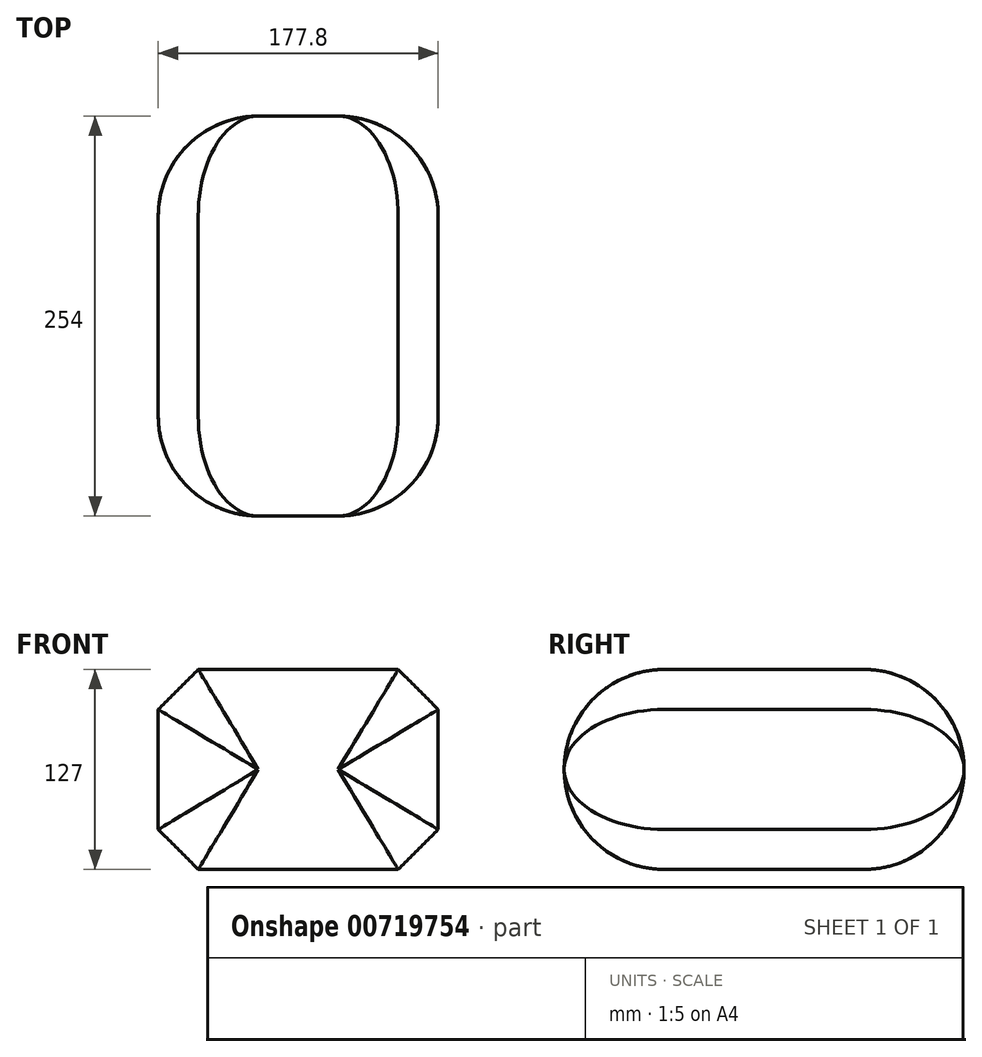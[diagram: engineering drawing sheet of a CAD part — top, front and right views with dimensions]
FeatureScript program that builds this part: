
annotation { "Feature Type Name" : "Feature", "Feature Type Description" : "" }
export const myFeature = defineFeature(function(context is Context, id is Id, definition is map)
    precondition{}
    {
        {
            var Q0;
            Q0=qCreatedBy(makeId("Front.planeOp"),FACE);
            var sketch = newSketch(context, id + "F0", { "sketchPlane" : qUnion([Q0])});
            skLineSegment(sketch, "E0.bottom", {"start": v(-177.8, 0) * mm, "end": v(0, 0) * mm});
            skLineSegment(sketch, "E0.top", {"start": v(-177.8, -127) * mm, "end": v(0, -127) * mm});
            skLineSegment(sketch, "E0.left", {"start": v(-177.8, 0) * mm, "end": v(-177.8, -127) * mm});
            skLineSegment(sketch, "E0.right", {"start": v(0, 0) * mm, "end": v(0, -127) * mm});
            skSolve(sketch);
        }
        {
            var Q0;
            Q0=makeQuery(id+"F0.imprint","IMPRINT",FACE,{"disambiguationData":[TD([[makeQuery(id+"F0.imprint","IMPRINT",EDGE,{"derivedFrom":sQuery(id+"F0.wireOp",EDGE,"E0.bottom")}),-1.0]])]});
            extrude(context, id + "F1", {"entities" : qUnion([Q0]), "depth" : 254 * mm, "offsetDistance" : 25.4 * mm});
        }
        {
            var Q0;
            Q0=makeQuery(id+"F1.opExtrude","CAP_FACE",FACE,{"disambiguationData":[OSD([sQuery(id+"F0.wireOp",EDGE,"E0.bottom"),sQuery(id+"F0.wireOp",EDGE,"E0.top"),sQuery(id+"F0.wireOp",EDGE,"E0.left"),sQuery(id+"F0.wireOp",EDGE,"E0.right")])],"isStart":false});
            var Q1;
            Q1=makeQuery(id+"F1.opExtrude","CAP_FACE",FACE,{"disambiguationData":[OSD([sQuery(id+"F0.wireOp",EDGE,"E0.bottom"),sQuery(id+"F0.wireOp",EDGE,"E0.top"),sQuery(id+"F0.wireOp",EDGE,"E0.left"),sQuery(id+"F0.wireOp",EDGE,"E0.right")])],"isStart":true});
            fillet(context, id + "F2", {"entities" : qUnion([Q0, Q1]), "radius" : 63.5 * mm, "tangentPropagation" : true, "allowEdgeOverflow" : false});
        }
        {
            var Q0;
            Q0=makeQuery(id+"F1.opExtrude","SWEPT_FACE",FACE,{"disambiguationData":[OSD([sQuery(id+"F0.wireOp",EDGE,"E0.right")])]});
            var Q1;
            Q1=makeQuery(id+"F1.opExtrude","SWEPT_FACE",FACE,{"disambiguationData":[OSD([sQuery(id+"F0.wireOp",EDGE,"E0.left")])]});
            var Q2;
            {var subQ0=sQuery(id+"F0.wireOp",EDGE,"E0.bottom");Q2=makeQuery(id+"F2.opFillet","BLEND_FACE",FACE,{"disambiguationData":[OSD([subQ0]),TDD([makeQuery(id+"F1.opExtrude","CAP_EDGE",EDGE,{"disambiguationData":[OSD([subQ0])],"isStart":false})])]});}
            var Q3;
            {var subQ0=sQuery(id+"F0.wireOp",EDGE,"E0.bottom");Q3=makeQuery(id+"F2.opFillet","BLEND_FACE",FACE,{"disambiguationData":[OSD([subQ0]),TDD([makeQuery(id+"F1.opExtrude","CAP_EDGE",EDGE,{"disambiguationData":[OSD([subQ0])],"isStart":true})])]});}
            chamfer(context, id + "F3", {"entities" : qUnion([Q0, Q1, Q2, Q3]), "width" : 25.4 * mm, "tangentPropagation" : true});
        }
    });
